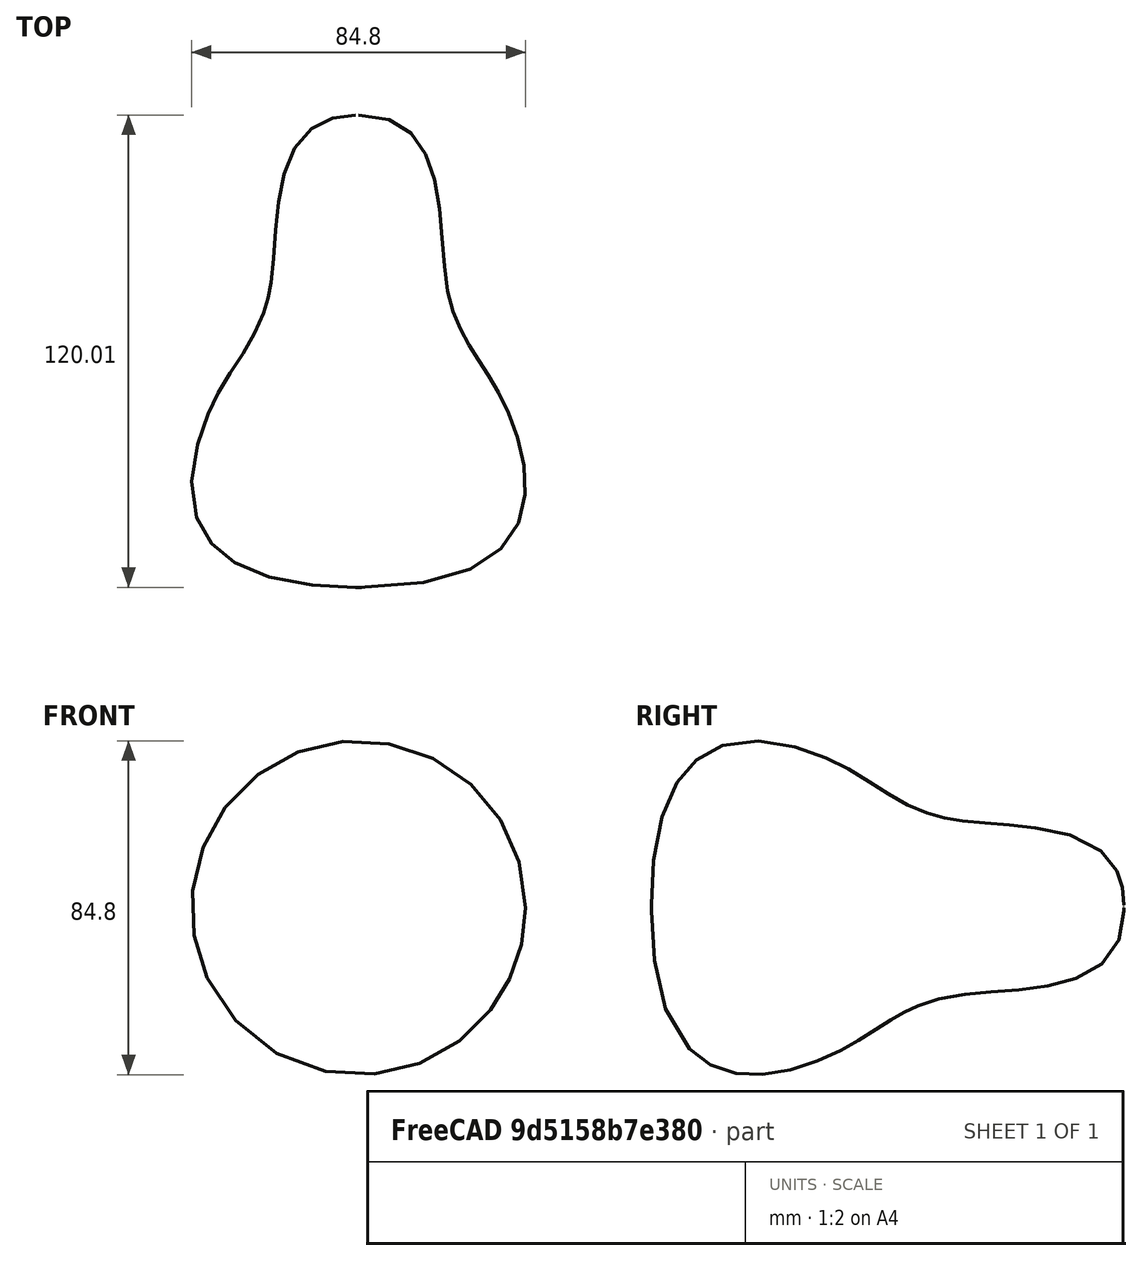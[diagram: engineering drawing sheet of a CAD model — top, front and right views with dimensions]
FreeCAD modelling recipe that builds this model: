
FCSTD DOCUMENT  (FreeCAD 0.18RUnknown)
Label: pear
License: All rights reserved
LicenseURL: http://en.wikipedia.org/wiki/All_rights_reserved
objects: Sketcher::SketchObject×1, PartDesign::Revolution×1, PartDesign::Body×1, Part::Plane×1, Part::MultiCommon×1
note: 6 computed .brp shape members not serialized (recipe doc carries the construction recipe); baked Part::Feature solids carry a one-line shape summary decoded from their .brp

FEATURE [Sketcher::SketchObject] Sketch
  sketch-geometry (12):
    g0-g5: Circle [constr] x6 (B-spline internal-alignment scaffolding for g6; pole/knot coordinates omitted)
    g6: BSplineCurve PolesCount=6 KnotsCount=4 Degree=3 IsPeriodic=0
    g7-g10: GeomPoint [constr] x4 (B-spline internal-alignment scaffolding for g6; pole/knot coordinates omitted)
    g11: LineSegment StartX=0 StartY=120 StartZ=0 EndX=0 EndY=0 EndZ=0
  constraints (9):
    c: Radius(g0) = 7
    c: Equal(g0, g1-g5) x5
    c: InternalAlignment(g0-g5 -> g6) x6
    c: InternalAlignment(g7-g10 -> g6) x4
    c: PointOnObject(g6,g-2)
    c: Coincident(g6,g-1)
    c: DistanceY(g6,g6) = 120
    c: Coincident(g11,g6)
    c: Coincident(g11,g6)
FEATURE [PartDesign::Revolution] Revolution
  Angle = 360
  Axis = (0,1,0)
  Base = (0,0,0)
  Profile = -> Sketch
  ReferenceAxis = -> Sketch [V_Axis]
  Reversed = true
FEATURE [PartDesign::Body] Body
  Group = -> [Sketch,Revolution]
  Origin = -> Origin
  Tip = -> Revolution
FEATURE [Part::Plane] Plane
  AttacherType = Attacher::AttachEngine3D
  Length = 120
  Width = 120
FEATURE [Part::MultiCommon] Common
  Shapes = -> [Plane,Revolution]
